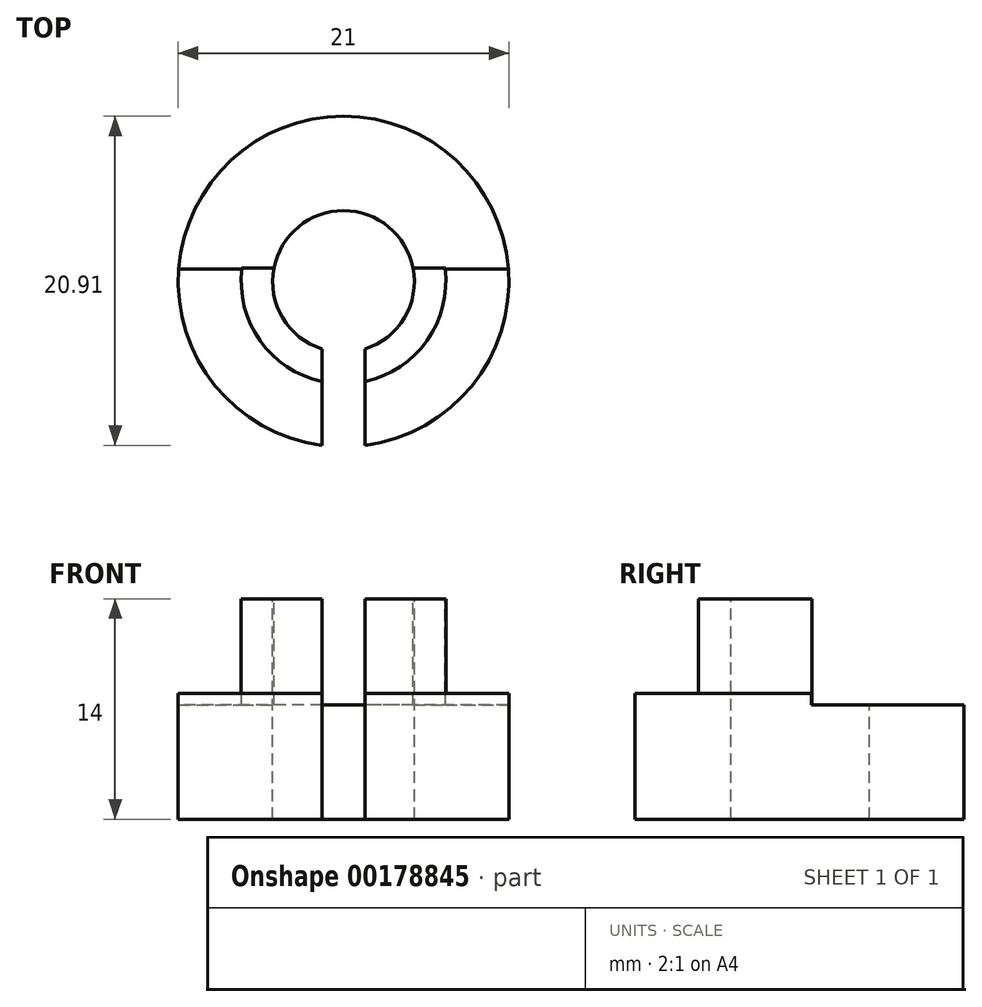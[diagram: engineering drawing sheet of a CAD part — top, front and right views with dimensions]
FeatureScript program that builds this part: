
annotation { "Feature Type Name" : "Feature", "Feature Type Description" : "" }
export const myFeature = defineFeature(function(context is Context, id is Id, definition is map)
    precondition{}
    {
        {
            var Q0;
            Q0=qCreatedBy(makeId("Top.planeOp"),FACE);
            var sketch = newSketch(context, id + "F0", { "sketchPlane" : qUnion([Q0])});
            skCircle(sketch, "E0", {"center": v(0, 0) * mm, "radius": 10.5 * mm});
            skSolve(sketch);
        }
        {
            var Q0;
            Q0 = qSketchRegion(id + "F0", true);
            extrude(context, id + "F1", {"entities" : qUnion([Q0]), "depth" : (8 + 6) * mm});
        }
        {
            var Q0;
            Q0=makeQuery(id+"F1.opExtrude","CAP_FACE",FACE,{"disambiguationData":[OSD([sQuery(id+"F0.wireOp",EDGE,"E0")])],"isStart":false});
            var sketch = newSketch(context, id + "F2", { "sketchPlane" : qUnion([Q0])});
            skCircle(sketch, "E1", {"center": v(0, 0) * mm, "radius": 6.5 * mm});
            skSolve(sketch);
        }
        {
            var Q0;
            Q0=makeQuery(id+"F2.imprint","IMPRINT",FACE,{"disambiguationData":[TD([[makeQuery(id+"F2.imprint","IMPRINT",EDGE,{"derivedFrom":sQuery(id+"F2.wireOp",EDGE,"E1")}),-1.0]])]});
            extrude(context, id + "F3", {"entities" : qUnion([Q0]), "operationType" : NewBodyOperationType.REMOVE, "oppositeDirection" : true, "depth" : 6 * mm});
        }
        {
            var Q0;
            Q0=makeQuery(id+"F1.opExtrude","CAP_FACE",FACE,{"disambiguationData":[OSD([sQuery(id+"F0.wireOp",EDGE,"E0")])],"isStart":false});
            var sketch = newSketch(context, id + "F4", { "sketchPlane" : qUnion([Q0])});
            skCircle(sketch, "E2", {"center": v(0, 0) * mm, "radius": 4.5 * mm});
            skSolve(sketch);
        }
        {
            var Q0;
            Q0=makeQuery(id+"F4.imprint","IMPRINT",FACE,{"disambiguationData":[TD([[makeQuery(id+"F4.imprint","IMPRINT",EDGE,{"derivedFrom":sQuery(id+"F4.wireOp",EDGE,"E2")}),1.0]])]});
            extrude(context, id + "F5", {"entities" : qUnion([Q0]), "operationType" : NewBodyOperationType.REMOVE, "endBound" : BoundingType.THROUGH_ALL, "oppositeDirection" : true, "depth" : 25 * mm});
        }
        {
            var Q0;
            Q0=qCreatedBy(makeId("Top.planeOp"),FACE);
            var sketch = newSketch(context, id + "F6", { "sketchPlane" : qUnion([Q0])});
            skLineSegment(sketch, "E3.bottom", {"start": v(1.36, -3.58) * mm, "end": v(-1.36, -3.58) * mm});
            skLineSegment(sketch, "E3.top", {"start": v(1.36, -11.16) * mm, "end": v(-1.36, -11.16) * mm});
            skLineSegment(sketch, "E3.left", {"start": v(1.36, -3.58) * mm, "end": v(1.36, -11.16) * mm});
            skLineSegment(sketch, "E3.right", {"start": v(-1.36, -3.58) * mm, "end": v(-1.36, -11.16) * mm});
            skPoint(sketch, "E3.middle", {"position": v(0, -7.37) * mm});
            skSolve(sketch);
        }
        {
            var Q0;
            Q0 = qSketchRegion(id + "F6", true);
            extrude(context, id + "F7", {"entities" : qUnion([Q0]), "operationType" : NewBodyOperationType.REMOVE, "endBound" : BoundingType.THROUGH_ALL, "depth" : 25 * mm});
        }
        {
            var Q0;
            Q0=makeQuery(id+"F1.opExtrude","CAP_FACE",FACE,{"disambiguationData":[OSD([sQuery(id+"F0.wireOp",EDGE,"E0")])],"isStart":false});
            var sketch = newSketch(context, id + "F8", { "sketchPlane" : qUnion([Q0])});
            skLineSegment(sketch, "E4.bottom", {"start": v(-10.98, 0.8) * mm, "end": v(-6.47, 0.8) * mm});
            skArc(sketch, "E5", {"start": v(10.98, 0.8) * mm, "mid": v(0, 11.01) * mm, "end": v(-10.98, 0.8) * mm});
            skArc(sketch, "E6", {"start": v(6.47, 0.8) * mm, "mid": v(0, 6.52) * mm, "end": v(-6.47, 0.8) * mm});
            skLineSegment(sketch, "E7.trimOffspring", {"start": v(6.47, 0.8) * mm, "end": v(10.98, 0.8) * mm});
            skSolve(sketch);
        }
        {
            var Q0;
            Q0 = qSketchRegion(id + "F8", true);
            extrude(context, id + "F9", {"entities" : qUnion([Q0]), "operationType" : NewBodyOperationType.REMOVE, "oppositeDirection" : true, "depth" : 6.75 * mm});
        }
        {
            var Q0;
            Q0=makeQuery(id+"F1.opExtrude","CAP_FACE",FACE,{"disambiguationData":[OSD([sQuery(id+"F0.wireOp",EDGE,"E0")])],"isStart":false});
            var sketch = newSketch(context, id + "F10", { "sketchPlane" : qUnion([Q0])});
            skLineSegment(sketch, "E8.bottom", {"start": v(-12, 11.94) * mm, "end": v(10.78, 11.94) * mm});
            skLineSegment(sketch, "E8.top", {"start": v(-12, 0.85) * mm, "end": v(10.78, 0.85) * mm});
            skLineSegment(sketch, "E8.left", {"start": v(-12, 11.94) * mm, "end": v(-12, 0.85) * mm});
            skLineSegment(sketch, "E8.right", {"start": v(10.78, 11.94) * mm, "end": v(10.78, 0.85) * mm});
            skSolve(sketch);
        }
        {
            var Q0;
            Q0 = qSketchRegion(id + "F10", true);
            extrude(context, id + "F11", {"entities" : qUnion([Q0]), "operationType" : NewBodyOperationType.REMOVE, "oppositeDirection" : true, "depth" : 6.75 * mm});
        }
    });
